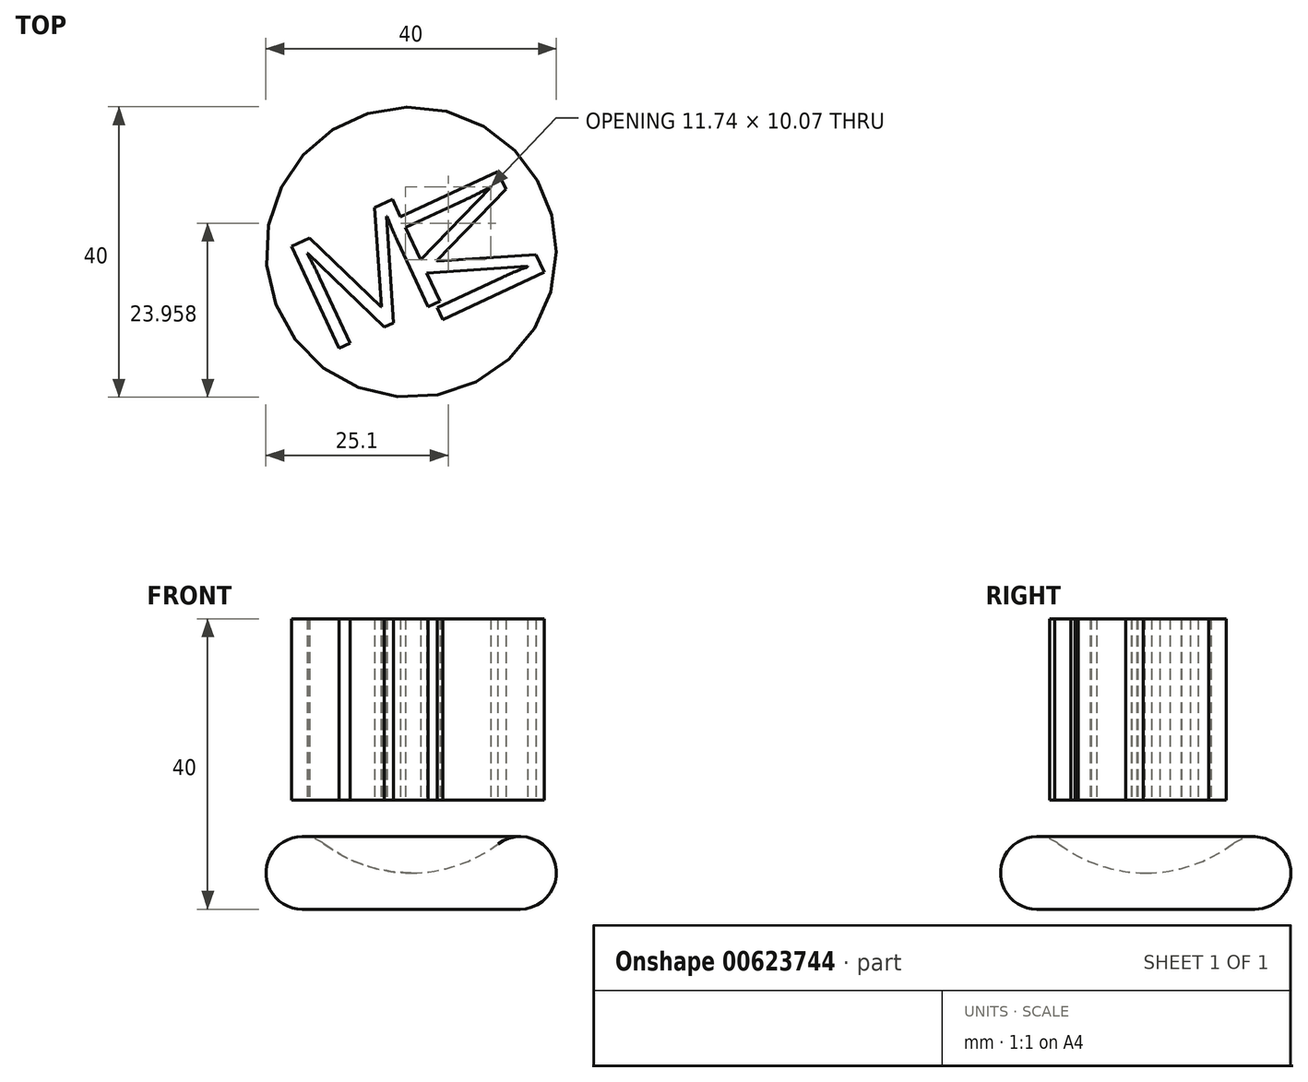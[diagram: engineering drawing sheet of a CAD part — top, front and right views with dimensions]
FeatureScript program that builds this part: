
annotation { "Feature Type Name" : "Feature", "Feature Type Description" : "" }
export const myFeature = defineFeature(function(context is Context, id is Id, definition is map)
    precondition{}
    {
        {
            var Q0;
            Q0=qCreatedBy(makeId("Front.planeOp"),FACE);
            var sketch = newSketch(context, id + "F0", { "sketchPlane" : qUnion([Q0])});
            skArc(sketch, "E0", {"start": v(-12, 9) * mm, "mid": v(-19.74, 6.58) * mm, "end": v(-15, 0) * mm});
            skLineSegment(sketch, "E1", {"start": v(0, 0) * mm, "end": v(-15, 0) * mm});
            skArc(sketch, "E2", {"start": v(-12, 9) * mm, "mid": v(-6.32, 6.03) * mm, "end": v(0, 5) * mm});
            skLineSegment(sketch, "E3", {"start": v(0, 5) * mm, "end": v(0, 0) * mm});
            skSolve(sketch);
        }
        {
            var Q0;
            Q0=makeQuery(id+"F0.imprint","IMPRINT",FACE,{"disambiguationData":[TD([[makeQuery(id+"F0.imprint","IMPRINT",EDGE,{"derivedFrom":sQuery(id+"F0.wireOp",EDGE,"E0")}),1.0]])]});
            var Q1;
            Q1=sQuery(id+"F0.wireOp",EDGE,"E3");
            revolve(context, id + "F1", {"entities" : qUnion([Q0]), "axis" : qUnion([Q1]), "revolveType" : RevolveType.FULL});
        }
        {
            var Q0;
            Q0=qCreatedBy(makeId("Top.planeOp"),FACE);
            cPlane(context, id + "F2", {"entities" : qUnion([Q0]), "cplaneType" : CPlaneType.OFFSET, "offset" : 15 * mm, "width" : 150 * mm, "height" : 150 * mm});
        }
        {
            var Q0;
            Q0=qCreatedBy(id+"F2.planeOp",FACE);
            var sketch = newSketch(context, id + "F3", { "sketchPlane" : qUnion([Q0])});
            skText(sketch, "E4", { "text": "M\n", "fontName": "OpenSans-Regular.ttf"});
            skText(sketch, "E5", { "text": "M\n", "fontName": "OpenSans-Regular.ttf"});
            const initialGuessF3  = {"E4": [-0.01184, -0.01412, 0.9063, 0.42262, 0.01558], "E5": [-0.00301, 0.0065, 0.42262, -0.9063, 0.01558]};
            skSetInitialGuess(sketch, initialGuessF3);
            skSolve(sketch);
        }
        {
            var Q0;
            Q0 = qSketchRegion(id + "F3", true);
            extrude(context, id + "F4", {"entities" : qUnion([Q0]), "depth" : 25 * mm, "offsetDistance" : 25 * mm});
        }
    });
